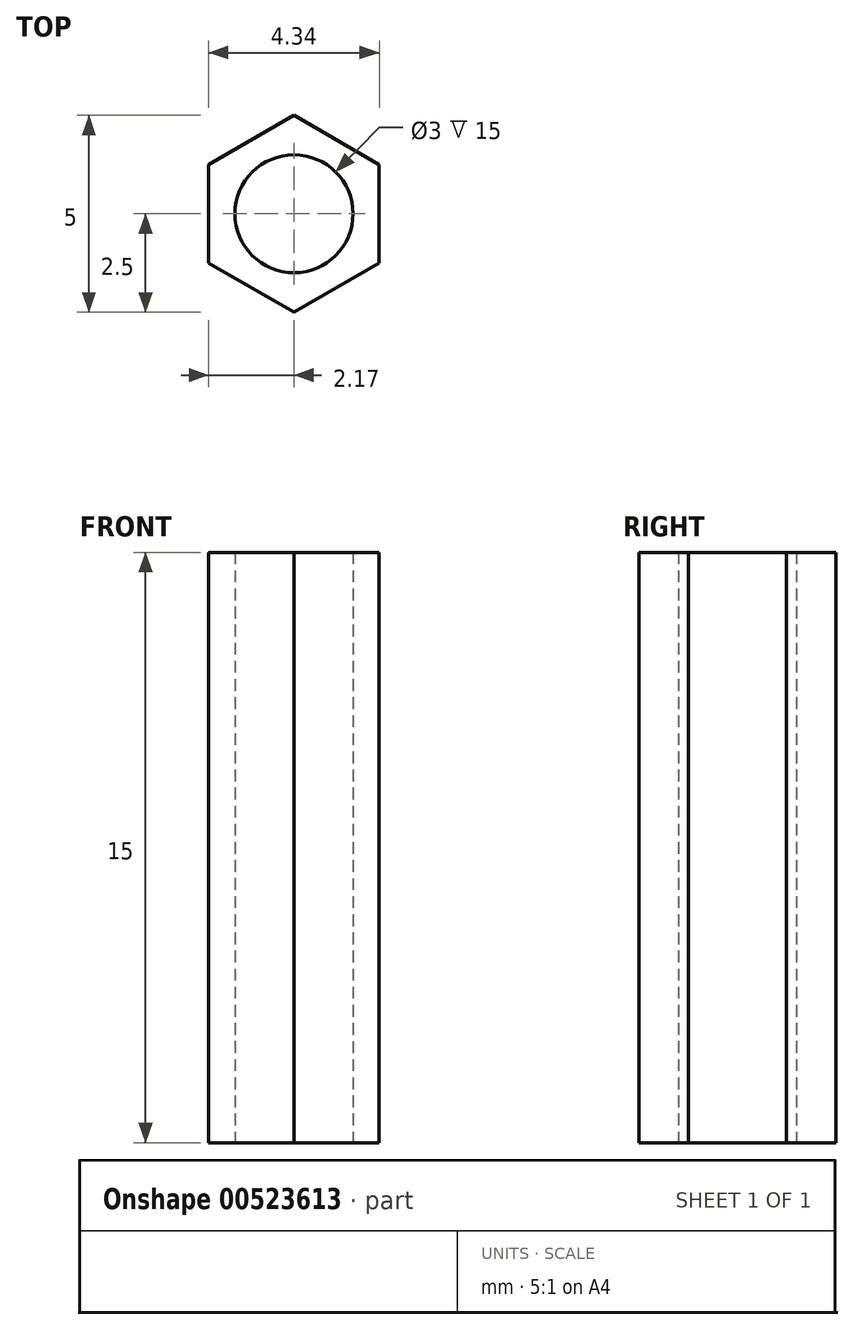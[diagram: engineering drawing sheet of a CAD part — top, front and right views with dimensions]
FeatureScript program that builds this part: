
annotation { "Feature Type Name" : "Feature", "Feature Type Description" : "" }
export const myFeature = defineFeature(function(context is Context, id is Id, definition is map)
    precondition{}
    {
        {
            var Q0;
            Q0=qCreatedBy(makeId("Top.planeOp"),FACE);
            var sketch = newSketch(context, id + "F0", { "sketchPlane" : qUnion([Q0])});
            skCircle(sketch, "E0.cCircle", {"center": v(0, 0) * mm, "radius": 2.5 * mm, "construction": true});
            skLineSegment(sketch, "E0.0", {"start": v(-2.17, -1.25) * mm, "end": v(-2.17, 1.25) * mm});
            skLineSegment(sketch, "E0.1", {"start": v(-2.17, 1.25) * mm, "end": v(0, 2.5) * mm});
            skLineSegment(sketch, "E0.2", {"start": v(0, 2.5) * mm, "end": v(2.17, 1.25) * mm});
            skLineSegment(sketch, "E0.3", {"start": v(2.17, 1.25) * mm, "end": v(2.17, -1.25) * mm});
            skLineSegment(sketch, "E0.4", {"start": v(2.17, -1.25) * mm, "end": v(0, -2.5) * mm});
            skLineSegment(sketch, "E0.5", {"start": v(0, -2.5) * mm, "end": v(-2.17, -1.25) * mm});
            skCircle(sketch, "E1", {"center": v(0, 0) * mm, "radius": 1.5 * mm});
            skSolve(sketch);
        }
        {
            var Q0;
            Q0 = qSketchRegion(id + "F0", true);
            extrude(context, id + "F1", {"entities" : qUnion([Q0]), "depth" : 15 * mm, "offsetDistance" : 25 * mm});
        }
    });
